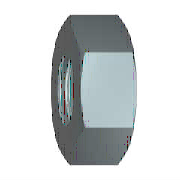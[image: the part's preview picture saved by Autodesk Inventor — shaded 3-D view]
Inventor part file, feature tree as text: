
AUTODESK INVENTOR PART (.ipt)
format: ipt  version: 2023 (Build 270158000, 158)  size: 165,376 bytes
history: native  units: mm (DEFAULTED — no unit token found)
features: sketch x3, other x2, extrude x1, hole x1, plane x1
ambient origin geometry x7: Origin, YZ Plane, XZ Plane, X Axis, Y Axis, Z Axis, Center Point
bodies: Solid1 (feature_tree)
feature tree (8):
  extrude  "Базовый элемент"  Depth=27.712813mm
  other  "Фаска1"
  hole  "Резьба"  [1 undecoded]
  other  "Work Axis1"
  plane  "Work Plane1"
  sketch  "Эскиз1"
  sketch  "Эскиз2"
  sketch  "Эскиз3"
note: 1 required parameter value undecoded (feature->parameter linkage not recoverable at this tier; creation-order binding heuristic only, values carry confidence <= 0.55)
